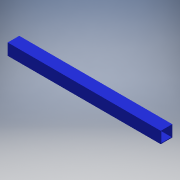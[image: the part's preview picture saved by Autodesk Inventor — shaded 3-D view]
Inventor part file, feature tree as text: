
AUTODESK INVENTOR PART (.ipt)
format: ipt  version: 2017 SP1 (Build 210196100, 196)  size: 97,792 bytes
history: native  units: in
note: dims shown in document units (in); Inventor stores cm internally (conversion verified against a paired STEP export)
features: extrude x1, sketch x1
ambient origin geometry x8: Origin, YZ Plane, XZ Plane, XY Plane, X Axis, Y Axis, Z Axis, Center Point
bodies: Solid1 (feature_tree)
feature tree (2):
  extrude  "Extrusion1"  Depth=0.0625in
  sketch  "Sketch1"  dims[d0=1.0in d1=0.0625in d2=13.25in d3=0.0in]
